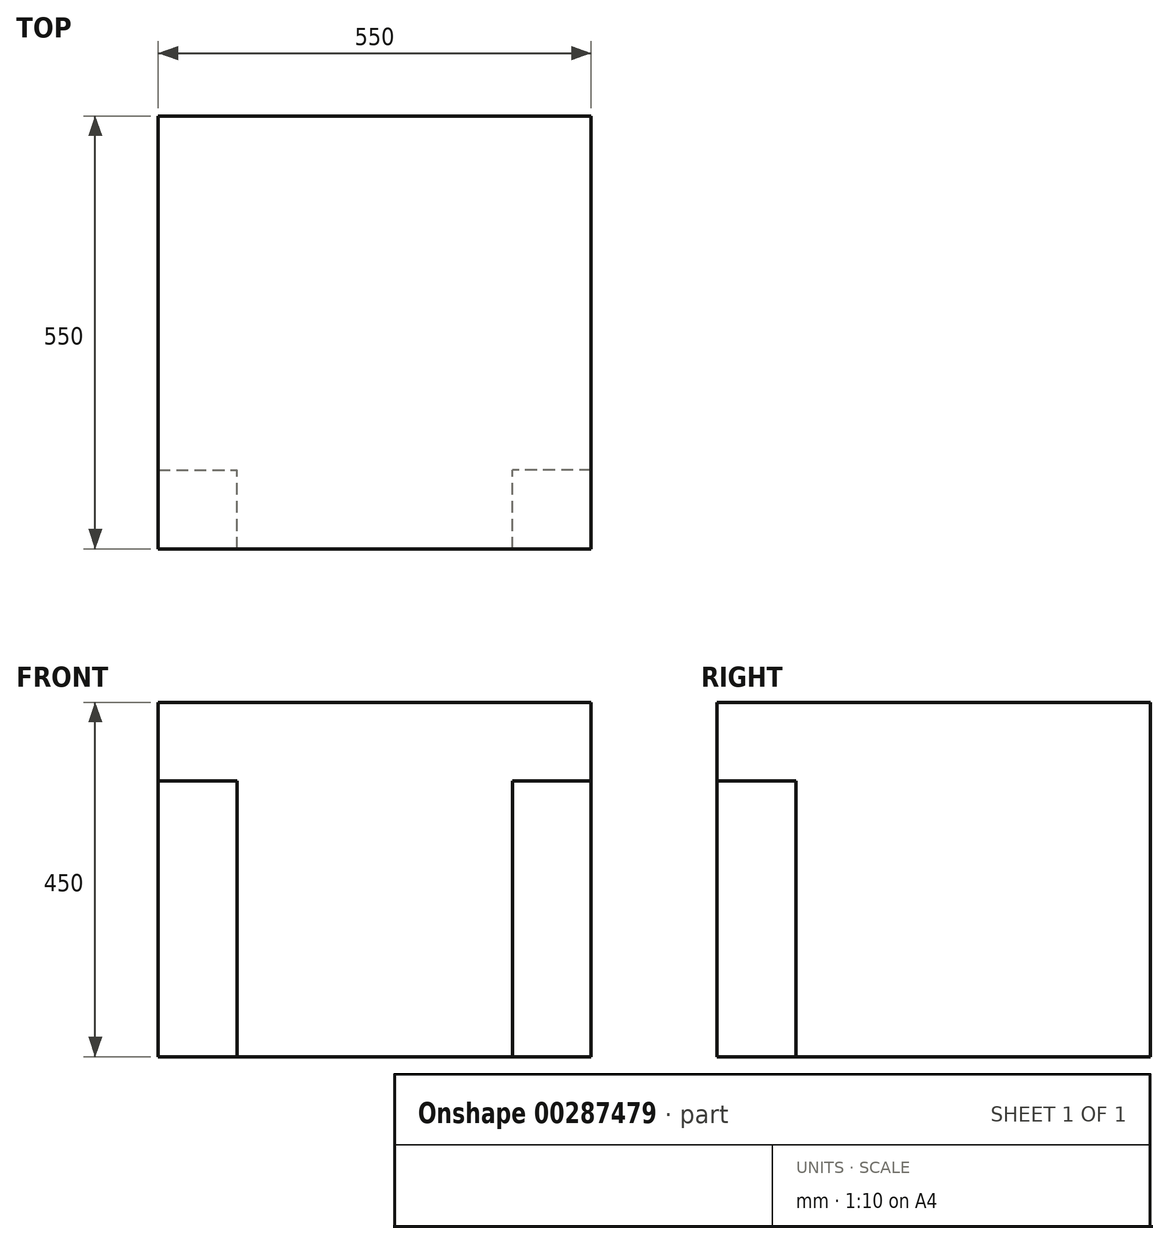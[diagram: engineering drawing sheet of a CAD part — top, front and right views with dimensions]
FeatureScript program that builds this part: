
annotation { "Feature Type Name" : "Feature", "Feature Type Description" : "" }
export const myFeature = defineFeature(function(context is Context, id is Id, definition is map)
    precondition{}
    {
        {
            var Q0;
            Q0=qCreatedBy(makeId("Top.planeOp"),FACE);
            var sketch = newSketch(context, id + "F0", { "sketchPlane" : qUnion([Q0])});
            skLineSegment(sketch, "E0.bottom", {"start": v(0, 0) * mm, "end": v(550, 0) * mm});
            skLineSegment(sketch, "E0.top", {"start": v(0, 550) * mm, "end": v(550, 550) * mm});
            skLineSegment(sketch, "E0.left", {"start": v(0, 0) * mm, "end": v(0, 550) * mm});
            skLineSegment(sketch, "E0.right", {"start": v(550, 0) * mm, "end": v(550, 550) * mm});
            skSolve(sketch);
        }
        {
            var Q0;
            Q0=qSketchRegion(id+"F0",true);
            extrude(context, id + "F1", {"entities" : qUnion([Q0]), "oppositeDirection" : true, "depth" : 450 * mm});
        }
        {
            var Q0;
            Q0=makeQuery(id+"F1.opExtrude","CAP_FACE",FACE,{"disambiguationData":[OSD([sQuery(id+"F0.wireOp",EDGE,"E0.bottom"),sQuery(id+"F0.wireOp",EDGE,"E0.top"),sQuery(id+"F0.wireOp",EDGE,"E0.left"),sQuery(id+"F0.wireOp",EDGE,"E0.right")])],"isStart":false});
            var sketch = newSketch(context, id + "F2", { "sketchPlane" : qUnion([Q0])});
            skLineSegment(sketch, "E1.bottom", {"start": v(0, 0) * mm, "end": v(550, 0) * mm});
            skLineSegment(sketch, "E1.top", {"start": v(0, -550) * mm, "end": v(550, -550) * mm});
            skLineSegment(sketch, "E1.left", {"start": v(0, 0) * mm, "end": v(0, -550) * mm});
            skLineSegment(sketch, "E1.right", {"start": v(550, 0) * mm, "end": v(550, -550) * mm});
            skLineSegment(sketch, "E2.bottom", {"start": v(0, 0) * mm, "end": v(100, 0) * mm});
            skLineSegment(sketch, "E2.top", {"start": v(0, -100) * mm, "end": v(100, -100) * mm});
            skLineSegment(sketch, "E2.left", {"start": v(0, 0) * mm, "end": v(0, -100) * mm});
            skLineSegment(sketch, "E2.right", {"start": v(100, 0) * mm, "end": v(100, -100) * mm});
            skLineSegment(sketch, "E3.bottom", {"start": v(550, 0) * mm, "end": v(450, 0) * mm});
            skLineSegment(sketch, "E3.top", {"start": v(550, -100) * mm, "end": v(450, -100) * mm});
            skLineSegment(sketch, "E3.left", {"start": v(550, 0) * mm, "end": v(550, -100) * mm});
            skLineSegment(sketch, "E3.right", {"start": v(450, 0) * mm, "end": v(450, -100) * mm});
            skLineSegment(sketch, "E4.bottom", {"start": v(550, -550) * mm, "end": v(450, -550) * mm});
            skLineSegment(sketch, "E4.top", {"start": v(550, -450) * mm, "end": v(450, -450) * mm});
            skLineSegment(sketch, "E4.left", {"start": v(550, -550) * mm, "end": v(550, -450) * mm});
            skLineSegment(sketch, "E4.right", {"start": v(450, -550) * mm, "end": v(450, -450) * mm});
            skLineSegment(sketch, "E5.bottom", {"start": v(0, -550) * mm, "end": v(100, -550) * mm});
            skLineSegment(sketch, "E5.top", {"start": v(0, -450) * mm, "end": v(100, -450) * mm});
            skLineSegment(sketch, "E5.left", {"start": v(0, -550) * mm, "end": v(0, -450) * mm});
            skLineSegment(sketch, "E5.right", {"start": v(100, -550) * mm, "end": v(100, -450) * mm});
            skSolve(sketch);
        }
        {
            var Q0;
            Q0=makeQuery(id+"F2.imprint","IMPRINT",FACE,{"disambiguationData":[TD([[makeQuery(id+"F2.imprint","IMPRINT",EDGE,{"derivedFrom":sQuery(id+"F2.wireOp",EDGE,"E1.bottom")}),-1.0]])]});
            extrude(context, id + "F3", {"entities" : qUnion([Q0]), "operationType" : NewBodyOperationType.REMOVE, "oppositeDirection" : true, "depth" : 350 * mm});
        }
    });
